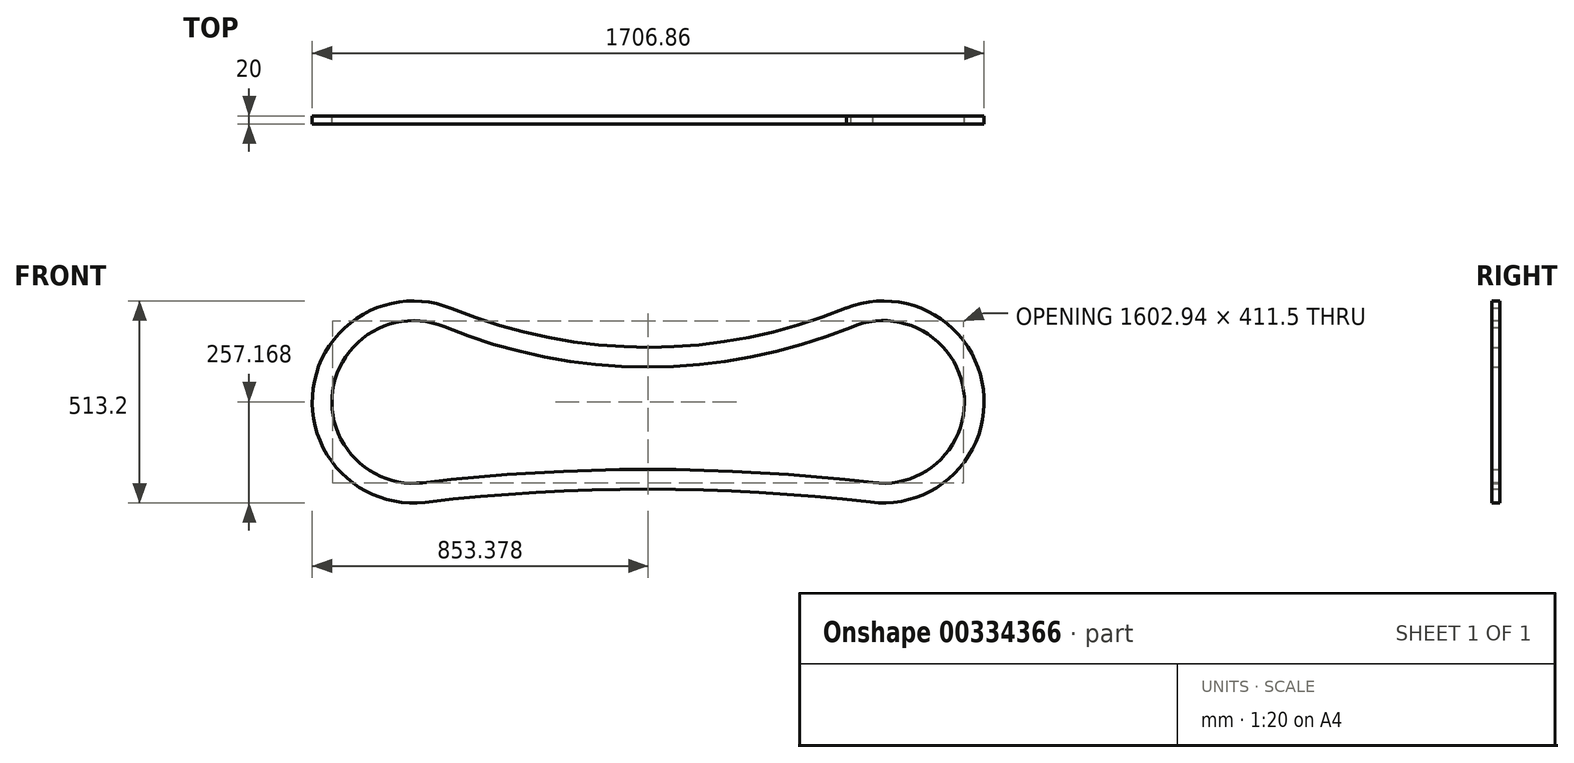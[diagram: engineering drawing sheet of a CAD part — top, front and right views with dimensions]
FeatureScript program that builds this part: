
annotation { "Feature Type Name" : "Feature", "Feature Type Description" : "" }
export const myFeature = defineFeature(function(context is Context, id is Id, definition is map)
    precondition{}
    {
        {
            var Q0;
            Q0=qCreatedBy(makeId("Front.planeOp"),FACE);
            var sketch = newSketch(context, id + "F0", { "sketchPlane" : qUnion([Q0])});
            skArc(sketch, "E0", {"start": v(-501.05, 250) * mm, "mid": v(-852.73, 47.47) * mm, "end": v(-568.51, -242.22) * mm});
            skArc(sketch, "E1", {"start": v(562.86, -241.94) * mm, "mid": v(849.8, 44.35) * mm, "end": v(501.38, 251.47) * mm});
            skArc(sketch, "E2", {"start": v(562.86, -241.94) * mm, "mid": v(-2.83, -208.97) * mm, "end": v(-568.51, -242.22) * mm});
            skPoint(sketch, "E2.centerSnap0", {"position": v(-1.62, -3.37) * mm});
            skArc(sketch, "E3", {"start": v(-501.05, 250) * mm, "mid": v(0.31, 151.47) * mm, "end": v(501.38, 251.47) * mm});
            skArc(sketch, "E4.0", {"start": v(-520.04, 203.74) * mm, "mid": v(-803.2, 40.68) * mm, "end": v(-574.36, -192.56) * mm});
            skArc(sketch, "E4.1", {"start": v(-520.04, 203.74) * mm, "mid": v(-3.46, 101.47) * mm, "end": v(513.39, 202.35) * mm});
            skArc(sketch, "E4.2", {"start": v(568.93, -192.3) * mm, "mid": v(799.75, 41.42) * mm, "end": v(513.39, 202.35) * mm});
            skArc(sketch, "E4.3", {"start": v(568.93, -192.3) * mm, "mid": v(-2.72, -158.97) * mm, "end": v(-574.36, -192.56) * mm});
            skSolve(sketch);
        }
        {
            var Q0;
            Q0=makeQuery(id+"F0.imprint","IMPRINT",FACE,{"disambiguationData":[TD([[makeQuery(id+"F0.imprint","IMPRINT",EDGE,{"derivedFrom":sQuery(id+"F0.wireOp",EDGE,"E0")}),1.0]])]});
            extrude(context, id + "F1", {"entities" : qUnion([Q0]), "depth" : 20 * mm});
        }
    });
